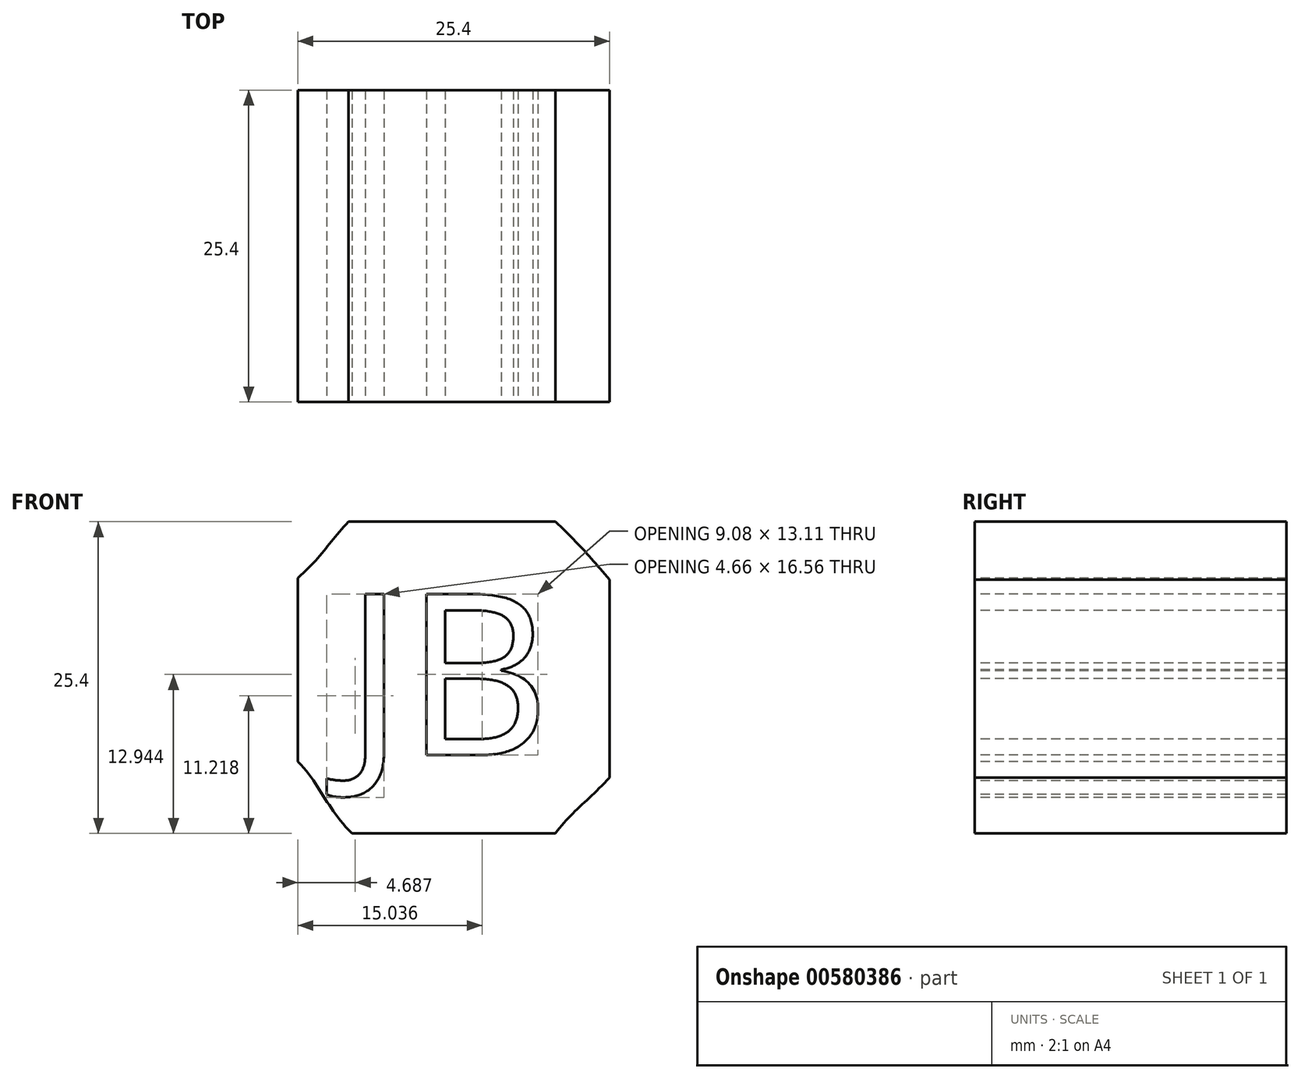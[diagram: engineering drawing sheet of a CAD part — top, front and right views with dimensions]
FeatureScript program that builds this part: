
annotation { "Feature Type Name" : "Feature", "Feature Type Description" : "" }
export const myFeature = defineFeature(function(context is Context, id is Id, definition is map)
    precondition{}
    {
        {
            var Q0;
            Q0=qCreatedBy(makeId("Front.planeOp"),FACE);
            var sketch = newSketch(context, id + "F0", { "sketchPlane" : qUnion([Q0])});
            skLineSegment(sketch, "E0.bottom", {"start": v(-37.6, -12.2) * mm, "end": v(-12.2, -12.2) * mm});
            skLineSegment(sketch, "E0.top", {"start": v(-37.6, -37.6) * mm, "end": v(-12.2, -37.6) * mm});
            skLineSegment(sketch, "E0.left", {"start": v(-37.6, -12.2) * mm, "end": v(-37.6, -37.6) * mm});
            skLineSegment(sketch, "E0.right", {"start": v(-12.2, -12.2) * mm, "end": v(-12.2, -37.6) * mm});
            skSolve(sketch);
        }
        {
            var Q0;
            Q0 = qSketchRegion(id + "F0", true);
            extrude(context, id + "F1", {"entities" : qUnion([Q0]), "depth" : 25.4 * mm, "offsetDistance" : 25.4 * mm});
        }
        {
            var Q0;
            Q0=makeQuery(id+"F1.opExtrude","CAP_FACE",FACE,{"disambiguationData":[OSD([sQuery(id+"F0.wireOp",EDGE,"E0.bottom"),sQuery(id+"F0.wireOp",EDGE,"E0.top"),sQuery(id+"F0.wireOp",EDGE,"E0.left"),sQuery(id+"F0.wireOp",EDGE,"E0.right")])],"isStart":false});
            var sketch = newSketch(context, id + "F2", { "sketchPlane" : qUnion([Q0])});
            skText(sketch, "E1", { "text": "JB", "fontName": "OpenSans-Regular.ttf"});
            const initialGuessF2  = {"E1": [-0.03381, -0.03121, 1, 0, 0.01322]};
            skSetInitialGuess(sketch, initialGuessF2);
            skSolve(sketch);
        }
        {
            var Q0;
            Q0 = qSketchRegion(id + "F2", true);
            extrude(context, id + "F3", {"entities" : qUnion([Q0]), "operationType" : NewBodyOperationType.REMOVE, "endBound" : BoundingType.THROUGH_ALL, "oppositeDirection" : true, "depth" : 25.4 * mm, "offsetDistance" : 25.4 * mm});
        }
        {
            var Q0;
            {var subQ0=sQuery(id+"F0.wireOp",EDGE,"E0.top");var subQ1=sQuery(id+"F0.wireOp",EDGE,"E0.right");var subQ2=sQuery(id+"F0.wireOp",EDGE,"E0.bottom");var subQ3=sQuery(id+"F0.wireOp",EDGE,"E0.left");Q0=makeQuery(id+"F3.boolean.opBoolean","SPLIT",FACE,{"disambiguationData":[TD([makeQuery(id+"F1.opExtrude","SWEPT_FACE",FACE,{"disambiguationData":[OSD([subQ2])]})])],"derivedFrom":makeQuery(id+"F1.opExtrude","CAP_FACE",FACE,{"disambiguationData":[OSD([subQ2,subQ0,subQ3,subQ1])],"isStart":false})});}
            var sketch = newSketch(context, id + "F4", { "sketchPlane" : qUnion([Q0])});
            skFitSpline(sketch, "E2", {"points": [v(-37.6, -16.78) * mm, v(-33.47, -12.2) * mm, v(-25.34, -7.63) * mm, v(-16.62, -12.2) * mm, v(-12.2, -16.93) * mm, v(-8.05, -24.48) * mm, v(-12.2, -33.05) * mm, v(-16.62, -37.6) * mm, v(-21.7, -42.64) * mm, v(-33.18, -37.6) * mm, v(-37.6, -31.75) * mm, v(-44.22, -24.05) * mm, v(-37.6, -16.78) * mm]});
            skSolve(sketch);
        }
        {
            var Q0;
            {var subQ0=sQuery(id+"F4.wireOp",EDGE,"E2");var subQ1=makeQuery(id+"F1.opExtrude","CAP_EDGE",EDGE,{"disambiguationData":[OSD([sQuery(id+"F0.wireOp",EDGE,"E0.bottom")])],"isStart":false});var subQ2=makeQuery(id+"F4.imprint","INTERSECT",VERTEX,{"disambiguationData":[OD(0.0)],"derivedFrom":[subQ1,subQ0]});Q0=makeQuery(id+"F4.imprint","IMPRINT",FACE,{"disambiguationData":[TD([[makeQuery(id+"F4.imprint","IMPRINT",EDGE,{"disambiguationData":[TD([[subQ2,-1.0]])],"derivedFrom":subQ0}),-1.0]])]});}
            var Q1;
            {var subQ0=sQuery(id+"F4.wireOp",EDGE,"E2");var subQ1=makeQuery(id+"F1.opExtrude","CAP_EDGE",EDGE,{"disambiguationData":[OSD([sQuery(id+"F0.wireOp",EDGE,"E0.right")])],"isStart":false});var subQ2=makeQuery(id+"F4.imprint","INTERSECT",VERTEX,{"disambiguationData":[OD(0.0)],"derivedFrom":[subQ1,subQ0]});Q1=makeQuery(id+"F4.imprint","IMPRINT",FACE,{"disambiguationData":[TD([[makeQuery(id+"F4.imprint","IMPRINT",EDGE,{"disambiguationData":[TD([[subQ2,-1.0]])],"derivedFrom":subQ0}),-1.0]])]});}
            var Q2;
            {var subQ0=sQuery(id+"F4.wireOp",EDGE,"E2");var subQ1=makeQuery(id+"F1.opExtrude","CAP_EDGE",EDGE,{"disambiguationData":[OSD([sQuery(id+"F0.wireOp",EDGE,"E0.bottom")])],"isStart":false});var subQ2=makeQuery(id+"F4.imprint","INTERSECT",VERTEX,{"disambiguationData":[OD(1.0)],"derivedFrom":[subQ1,subQ0]});Q2=makeQuery(id+"F4.imprint","IMPRINT",FACE,{"disambiguationData":[TD([[makeQuery(id+"F4.imprint","IMPRINT",EDGE,{"disambiguationData":[TD([[subQ2,-1.0]])],"derivedFrom":subQ0}),1.0]])]});}
            var Q3;
            {var subQ0=sQuery(id+"F4.wireOp",EDGE,"E2");var subQ1=makeQuery(id+"F1.opExtrude","CAP_EDGE",EDGE,{"disambiguationData":[OSD([sQuery(id+"F0.wireOp",EDGE,"E0.bottom")])],"isStart":false});var subQ2=makeQuery(id+"F4.imprint","INTERSECT",VERTEX,{"disambiguationData":[OD(0.0)],"derivedFrom":[subQ1,subQ0]});Q3=makeQuery(id+"F4.imprint","IMPRINT",FACE,{"disambiguationData":[TD([[makeQuery(id+"F4.imprint","IMPRINT",EDGE,{"disambiguationData":[TD([[subQ2,1.0]])],"derivedFrom":subQ0}),1.0]])]});}
            var Q4;
            {var subQ0=sQuery(id+"F4.wireOp",EDGE,"E2");var subQ1=makeQuery(id+"F1.opExtrude","CAP_EDGE",EDGE,{"disambiguationData":[OSD([sQuery(id+"F0.wireOp",EDGE,"E0.left")])],"isStart":false});var subQ2=makeQuery(id+"F4.imprint","INTERSECT",VERTEX,{"disambiguationData":[OD(0.0)],"derivedFrom":[subQ1,subQ0]});Q4=makeQuery(id+"F4.imprint","IMPRINT",FACE,{"disambiguationData":[TD([[makeQuery(id+"F4.imprint","IMPRINT",EDGE,{"disambiguationData":[TD([[subQ2,1.0]])],"derivedFrom":subQ0}),-1.0]])]});}
            var Q5;
            {var subQ0=sQuery(id+"F4.wireOp",EDGE,"E2");var subQ1=makeQuery(id+"F1.opExtrude","CAP_EDGE",EDGE,{"disambiguationData":[OSD([sQuery(id+"F0.wireOp",EDGE,"E0.top")])],"isStart":false});var subQ2=makeQuery(id+"F4.imprint","INTERSECT",VERTEX,{"disambiguationData":[OD(0.0)],"derivedFrom":[subQ1,subQ0]});Q5=makeQuery(id+"F4.imprint","IMPRINT",FACE,{"disambiguationData":[TD([[makeQuery(id+"F4.imprint","IMPRINT",EDGE,{"disambiguationData":[TD([[subQ2,-1.0]])],"derivedFrom":subQ0}),-1.0]])]});}
            var Q6;
            {var subQ0=sQuery(id+"F4.wireOp",EDGE,"E2");var subQ1=makeQuery(id+"F1.opExtrude","CAP_EDGE",EDGE,{"disambiguationData":[OSD([sQuery(id+"F0.wireOp",EDGE,"E0.top")])],"isStart":false});var subQ2=makeQuery(id+"F4.imprint","INTERSECT",VERTEX,{"disambiguationData":[OD(1.0)],"derivedFrom":[subQ1,subQ0]});Q6=makeQuery(id+"F4.imprint","IMPRINT",FACE,{"disambiguationData":[TD([[makeQuery(id+"F4.imprint","IMPRINT",EDGE,{"disambiguationData":[TD([[subQ2,-1.0]])],"derivedFrom":subQ0}),1.0]])]});}
            var Q7;
            {var subQ0=sQuery(id+"F4.wireOp",EDGE,"E2");var subQ1=makeQuery(id+"F1.opExtrude","CAP_EDGE",EDGE,{"disambiguationData":[OSD([sQuery(id+"F0.wireOp",EDGE,"E0.right")])],"isStart":false});var subQ2=makeQuery(id+"F4.imprint","INTERSECT",VERTEX,{"disambiguationData":[OD(1.0)],"derivedFrom":[subQ1,subQ0]});Q7=makeQuery(id+"F4.imprint","IMPRINT",FACE,{"disambiguationData":[TD([[makeQuery(id+"F4.imprint","IMPRINT",EDGE,{"disambiguationData":[TD([[subQ2,-1.0]])],"derivedFrom":subQ0}),1.0]])]});}
            extrude(context, id + "F5", {"entities" : qUnion([Q0, Q1, Q2, Q3, Q4, Q5, Q6, Q7]), "operationType" : NewBodyOperationType.REMOVE, "endBound" : BoundingType.THROUGH_ALL, "oppositeDirection" : true, "depth" : 25.4 * mm, "offsetDistance" : 25.4 * mm});
        }
    });
